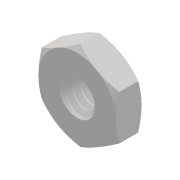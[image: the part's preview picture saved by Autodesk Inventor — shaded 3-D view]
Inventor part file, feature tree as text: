
AUTODESK INVENTOR PART (.ipt)
format: ipt  version: 2018 (Build 220112000, 112)  size: 281,088 bytes
history: native  units: mm
features: mirror x1
ambient origin geometry x8: Origin, YZ Plane, XZ Plane, XY Plane, X Axis, Y Axis, Z Axis, Center Point
bodies: Solid1 (feature_tree)
feature tree (1):
  mirror  "Mirror1"
